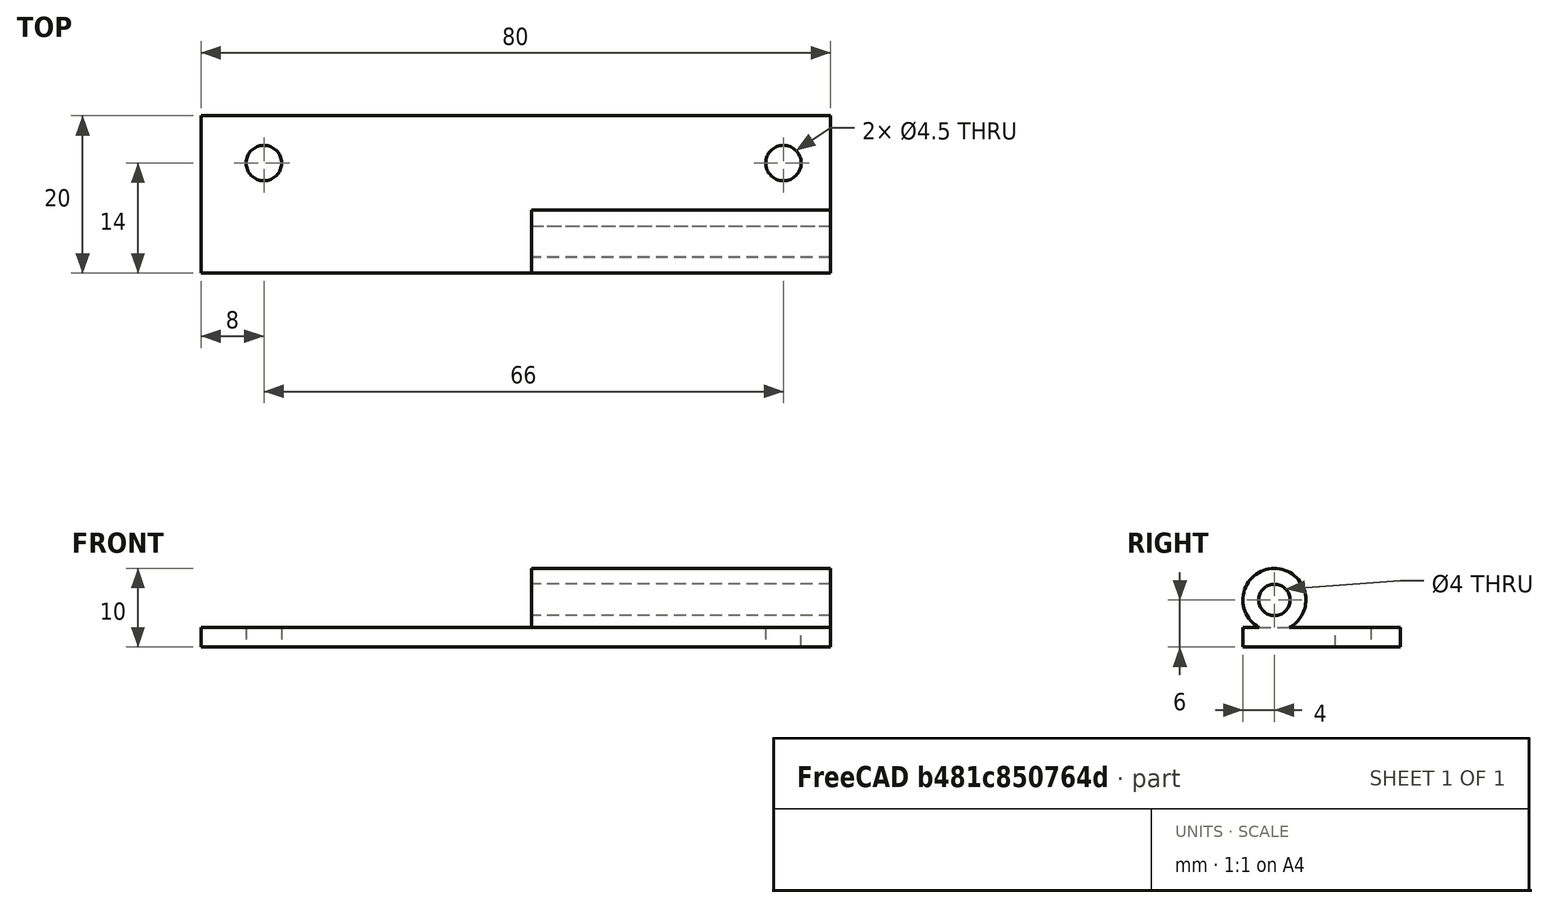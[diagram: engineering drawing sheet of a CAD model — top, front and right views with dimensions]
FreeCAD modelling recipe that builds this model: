
FCSTD DOCUMENT  (FreeCAD 0.21R33668 +26 (Git))
Label: 1-folding-hinge
License: All rights reserved
LicenseURL: http://en.wikipedia.org/wiki/All_rights_reserved
objects: PartDesign::SubtractiveCylinder×3, PartDesign::AdditiveBox×1, PartDesign::AdditiveCylinder×1, PartDesign::Body×1
note: 11 computed .brp shape members not serialized (recipe doc carries the construction recipe); baked Part::Feature solids carry a one-line shape summary decoded from their .brp

FEATURE [PartDesign::AdditiveBox] Box
  AttacherType = Attacher::AttachEngine3D
  Height = 2.5
  Length = 80
  Width = 20
FEATURE [PartDesign::AdditiveCylinder] Cylinder
  Angle = 360
  AttacherType = Attacher::AttachEngine3D
  AttachmentOffset = pos=(4,6,-38) rot=(0,0,1;0rad)
  BaseFeature = -> Box
  FirstAngle = 0
  Height = 38
  MapMode = 5
  Placement = pos=(42,4,6) rot=(0.57735,0.57735,0.57735;2.0944rad)
  Radius = 4
  SecondAngle = 0
  Support = -> [Box]
FEATURE [PartDesign::SubtractiveCylinder] Cylinder001  label="pin-slide"
  Angle = 360
  AttacherType = Attacher::AttachEngine3D
  AttachmentOffset = pos=(0,0,-38) rot=(0,0,1;0rad)
  BaseFeature = -> Cylinder
  FirstAngle = 0
  Height = 38
  MapMode = 5
  Placement = pos=(42,4,6) rot=(0.57735,0.57735,0.57735;2.0944rad)
  Radius = 2
  SecondAngle = 0
  Support = -> [Cylinder]
FEATURE [PartDesign::SubtractiveCylinder] Cylinder002  label="mp1"
  Angle = 360
  AttacherType = Attacher::AttachEngine3D
  AttachmentOffset = pos=(-10,-34,-2.5) rot=(0,0,1;0rad)
  BaseFeature = -> Cylinder001
  FirstAngle = 0
  Height = 2.5
  MapMode = 5
  Placement = pos=(8,14,-6.7e-15) rot=(0,0,-1;1.5708rad)
  Radius = 2.25
  SecondAngle = 0
  Support = -> [Cylinder001]
FEATURE [PartDesign::SubtractiveCylinder] Cylinder003  label="mp2"
  Angle = 360
  AttacherType = Attacher::AttachEngine3D
  AttachmentOffset = pos=(66,0,-2.5) rot=(0,0,1;0rad)
  BaseFeature = -> Cylinder002
  FirstAngle = 0
  Height = 2.5
  MapMode = 11
  Placement = pos=(74,14,-6.7e-15) rot=(0,0,1;0rad)
  Radius = 2.25
  SecondAngle = 0
  Support = -> [Cylinder002]
FEATURE [PartDesign::Body] Body
  Group = -> [Box,Cylinder,Cylinder001,Cylinder002,Cylinder003]
  Origin = -> Origin
  Tip = -> Cylinder003
